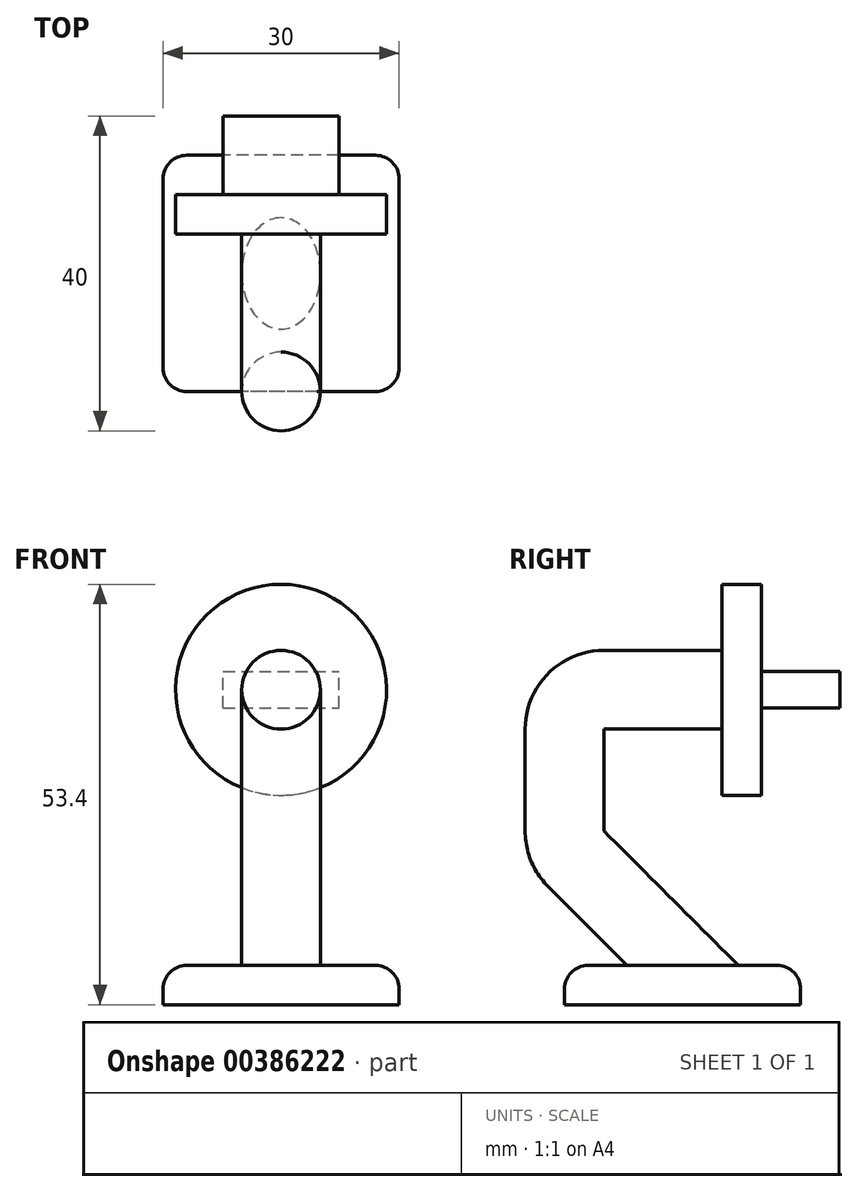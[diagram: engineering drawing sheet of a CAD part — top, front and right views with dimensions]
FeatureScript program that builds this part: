
annotation { "Feature Type Name" : "Feature", "Feature Type Description" : "" }
export const myFeature = defineFeature(function(context is Context, id is Id, definition is map)
    precondition{}
    {
        {
            var Q0;
            Q0=qCreatedBy(makeId("Front.planeOp"),FACE);
            var sketch = newSketch(context, id + "F0", { "sketchPlane" : qUnion([Q0])});
            skCircle(sketch, "E0", {"center": v(0, 0) * mm, "radius": 5 * mm});
            skCircle(sketch, "E1", {"center": v(0, 0) * mm, "radius": 13.4 * mm});
            skSolve(sketch);
        }
        {
            var Q0;
            Q0=qCreatedBy(makeId("Right.planeOp"),FACE);
            var sketch = newSketch(context, id + "F1", { "sketchPlane" : qUnion([Q0])});
            skLineSegment(sketch, "E2", {"start": v(0, 0) * mm, "end": v(-15, 0) * mm});
            skLineSegment(sketch, "E3", {"start": v(-20, -5) * mm, "end": v(-20, -17.93) * mm});
            skLineSegment(sketch, "E4", {"start": v(-20, -20) * mm, "end": v(-20, -35) * mm});
            skLineSegment(sketch, "E5", {"start": v(-20, -35) * mm, "end": v(-5, -35) * mm});
            skLineSegment(sketch, "E6", {"start": v(-18.54, -21.46) * mm, "end": v(-5, -35) * mm});
            skLineSegment(sketch, "E7", {"start": v(-5, -35) * mm, "end": v(10, -35) * mm});
            skLineSegment(sketch, "E8", {"start": v(10, -35) * mm, "end": v(10, -40) * mm});
            skLineSegment(sketch, "E9", {"start": v(10, -40) * mm, "end": v(-20, -40) * mm});
            skLineSegment(sketch, "E10", {"start": v(-20, -40) * mm, "end": v(-20, -35) * mm});
            skPoint(sketch, "E11.visualSharp", {"position": v(-20, 0) * mm});
            skArc(sketch, "E11.filletArc", {"start": v(-15, 0) * mm, "mid": v(-18.54, -1.46) * mm, "end": v(-20, -5) * mm});
            skPoint(sketch, "E12.visualSharp", {"position": v(-20, -20) * mm});
            skArc(sketch, "E12.filletArc", {"start": v(-20, -17.93) * mm, "mid": v(-19.62, -19.84) * mm, "end": v(-18.54, -21.46) * mm});
            skLineSegment(sketch, "E13", {"start": v(-5, -35) * mm, "end": v(-0.99, -39.01) * mm});
            skSolve(sketch);
        }
        {
            var Q0;
            Q0=qCreatedBy(makeId("Front.planeOp"),FACE);
            var sketch = newSketch(context, id + "F2", { "sketchPlane" : qUnion([Q0])});
            skLineSegment(sketch, "E14.bottom", {"start": v(-7.35, -2.3) * mm, "end": v(7.35, -2.3) * mm});
            skLineSegment(sketch, "E14.top", {"start": v(-7.35, 2.3) * mm, "end": v(7.35, 2.3) * mm});
            skLineSegment(sketch, "E14.left", {"start": v(-7.35, -2.3) * mm, "end": v(-7.35, 2.3) * mm});
            skLineSegment(sketch, "E14.right", {"start": v(7.35, -2.3) * mm, "end": v(7.35, 2.3) * mm});
            skPoint(sketch, "E14.middle", {"position": v(0, 0) * mm});
            skSolve(sketch);
        }
        {
            var Q0;
            Q0=makeQuery(id+"F0.imprint","IMPRINT",FACE,{"disambiguationData":[TD([[makeQuery(id+"F0.imprint","IMPRINT",EDGE,{"derivedFrom":sQuery(id+"F0.wireOp",EDGE,"E0")}),-1.0]])]});
            var Q1;
            Q1=makeQuery(id+"F0.imprint","IMPRINT",FACE,{"disambiguationData":[TD([[makeQuery(id+"F0.imprint","IMPRINT",EDGE,{"derivedFrom":sQuery(id+"F0.wireOp",EDGE,"E0")}),1.0]])]});
            extrude(context, id + "F3", {"entities" : qUnion([Q0, Q1]), "oppositeDirection" : true, "depth" : 5 * mm});
        }
        {
            var Q0;
            Q0=makeQuery(id+"F2.imprint","IMPRINT",FACE,{"disambiguationData":[TD([[makeQuery(id+"F2.imprint","IMPRINT",EDGE,{"derivedFrom":sQuery(id+"F2.wireOp",EDGE,"E14.bottom")}),1.0]])]});
            extrude(context, id + "F4", {"entities" : qUnion([Q0]), "operationType" : NewBodyOperationType.ADD, "oppositeDirection" : true, "depth" : 15 * mm});
        }
        {
            var Q0;
            Q0=makeQuery(id+"F1.imprint","IMPRINT",FACE,{"disambiguationData":[TD([[makeQuery(id+"F1.imprint","IMPRINT",EDGE,{"derivedFrom":sQuery(id+"F1.wireOp",EDGE,"E5")}),-1.0]])]});
            extrude(context, id + "F5", {"entities" : qUnion([Q0]), "endBound" : BoundingType.SYMMETRIC, "depth" : 30 * mm});
        }
        {
            var Q0;
            Q0=makeQuery(id+"F0.imprint","IMPRINT",FACE,{"disambiguationData":[TD([[makeQuery(id+"F0.imprint","IMPRINT",EDGE,{"derivedFrom":sQuery(id+"F0.wireOp",EDGE,"E0")}),1.0]])]});
            var Q1;
            Q1=sQuery(id+"F1.wireOp",EDGE,"E2");
            var Q2;
            Q2=sQuery(id+"F1.wireOp",EDGE,"E11.filletArc");
            var Q3;
            Q3=sQuery(id+"F1.wireOp",EDGE,"E3");
            var Q4;
            Q4=sQuery(id+"F1.wireOp",EDGE,"E12.filletArc");
            var Q5;
            Q5=sQuery(id+"F1.wireOp",EDGE,"E6");
            var Q6;
            Q6=sQuery(id+"F1.wireOp",EDGE,"E13");
            sweep(context, id + "F6", {"profiles" : qUnion([Q0]), "path" : qUnion([Q1, Q2, Q3, Q4, Q5, Q6])});
        }
        {
            var Q0;
            Q0=makeQuery(id+"F3.opExtrude","SWEPT_BODY",BODY,{"disambiguationData":[OSD([sQuery(id+"F0.wireOp",EDGE,"E1")])]});
            var Q1;
            Q1=makeQuery(id+"F5.opExtrude","SWEPT_BODY",BODY,{"disambiguationData":[OSD([sQuery(id+"F1.wireOp",EDGE,"E5"),sQuery(id+"F1.wireOp",EDGE,"E7"),sQuery(id+"F1.wireOp",EDGE,"E8"),sQuery(id+"F1.wireOp",EDGE,"E9"),sQuery(id+"F1.wireOp",EDGE,"E10")])]});
            var Q2;
            Q2=makeQuery(id+"F6.opSweep","SWEPT_BODY",BODY,{"disambiguationData":[OSD([sQuery(id+"F0.wireOp",EDGE,"E0"),sQuery(id+"F1.wireOp",EDGE,"E13")])]});
            booleanBodies(context, id + "F7", {"operationType" : BooleanOperationType.UNION, "tools" : qUnion([Q0, Q1, Q2])});
        }
        {
            var Q0;
            Q0=makeQuery(id+"F5.opExtrude","SWEPT_FACE",FACE,{"disambiguationData":[OSD([sQuery(id+"F1.wireOp",EDGE,"E9")])]});
            var sketch = newSketch(context, id + "F8", { "sketchPlane" : qUnion([Q0])});
            skLineSegment(sketch, "E15.bottom", {"start": v(7.82, 10.31) * mm, "end": v(-7.82, 10.31) * mm});
            skLineSegment(sketch, "E15.top", {"start": v(7.82, -2.5) * mm, "end": v(-7.82, -2.5) * mm});
            skLineSegment(sketch, "E15.left", {"start": v(7.82, 10.31) * mm, "end": v(7.82, -2.5) * mm});
            skLineSegment(sketch, "E15.right", {"start": v(-7.82, 10.31) * mm, "end": v(-7.82, -2.5) * mm});
            skPoint(sketch, "E15.middle", {"position": v(0, 3.9) * mm});
            skPoint(sketch, "E15.middle.positionSnap0", {"position": v(0, 1.97) * mm});
            skPoint(sketch, "E15.centerSnap0", {"position": v(0, 1.97) * mm});
            skSolve(sketch);
        }
        {
            var Q0;
            Q0=makeQuery(id+"F8.imprint","IMPRINT",FACE,{"disambiguationData":[TD([[makeQuery(id+"F8.imprint","IMPRINT",EDGE,{"derivedFrom":sQuery(id+"F8.wireOp",EDGE,"E15.bottom")}),1.0]])]});
            extrude(context, id + "F9", {"entities" : qUnion([Q0]), "operationType" : NewBodyOperationType.ADD, "depth" : 25 * mm});
        }
        {
            var Q0;
            Q0=makeQuery(id+"F9.opExtrude","SWEPT_FACE",FACE,{"disambiguationData":[OSD([sQuery(id+"F8.wireOp",EDGE,"E15.top")])]});
            extrude(context, id + "F10", {"entities" : qUnion([Q0]), "operationType" : NewBodyOperationType.REMOVE, "oppositeDirection" : true, "depth" : 25 * mm});
        }
        {
            var Q0;
            Q0=makeQuery(id+"F5.opExtrude","CAP_EDGE",EDGE,{"disambiguationData":[OSD([sQuery(id+"F1.wireOp",EDGE,"E5"),sQuery(id+"F1.wireOp",EDGE,"E7")])],"isStart":true});
            var Q1;
            Q1=makeQuery(id+"F5.opExtrude","SWEPT_EDGE",EDGE,{"disambiguationData":[OSD([sQuery(id+"F1.wireOp",EDGE,"E7"),sQuery(id+"F1.wireOp",EDGE,"E8")])]});
            var Q2;
            Q2=makeQuery(id+"F5.opExtrude","CAP_EDGE",EDGE,{"disambiguationData":[OSD([sQuery(id+"F1.wireOp",EDGE,"E5"),sQuery(id+"F1.wireOp",EDGE,"E7")])],"isStart":false});
            var Q3;
            Q3=makeQuery(id+"F5.opExtrude","SWEPT_EDGE",EDGE,{"disambiguationData":[OSD([sQuery(id+"F1.wireOp",EDGE,"E5"),sQuery(id+"F1.wireOp",EDGE,"E10")])]});
            var Q4;
            Q4=makeQuery(id+"F5.opExtrude","CAP_EDGE",EDGE,{"disambiguationData":[OSD([sQuery(id+"F1.wireOp",EDGE,"E10")])],"isStart":false});
            var Q5;
            Q5=makeQuery(id+"F5.opExtrude","CAP_EDGE",EDGE,{"disambiguationData":[OSD([sQuery(id+"F1.wireOp",EDGE,"E10")])],"isStart":true});
            var Q6;
            Q6=makeQuery(id+"F5.opExtrude","CAP_EDGE",EDGE,{"disambiguationData":[OSD([sQuery(id+"F1.wireOp",EDGE,"E8")])],"isStart":true});
            var Q7;
            Q7=makeQuery(id+"F5.opExtrude","CAP_EDGE",EDGE,{"disambiguationData":[OSD([sQuery(id+"F1.wireOp",EDGE,"E8")])],"isStart":false});
            fillet(context, id + "F11", {"entities" : qUnion([Q0, Q1, Q2, Q3, Q4, Q5, Q6, Q7]), "radius" : 3 * mm, "tangentPropagation" : true, "allowEdgeOverflow" : false});
        }
    });
